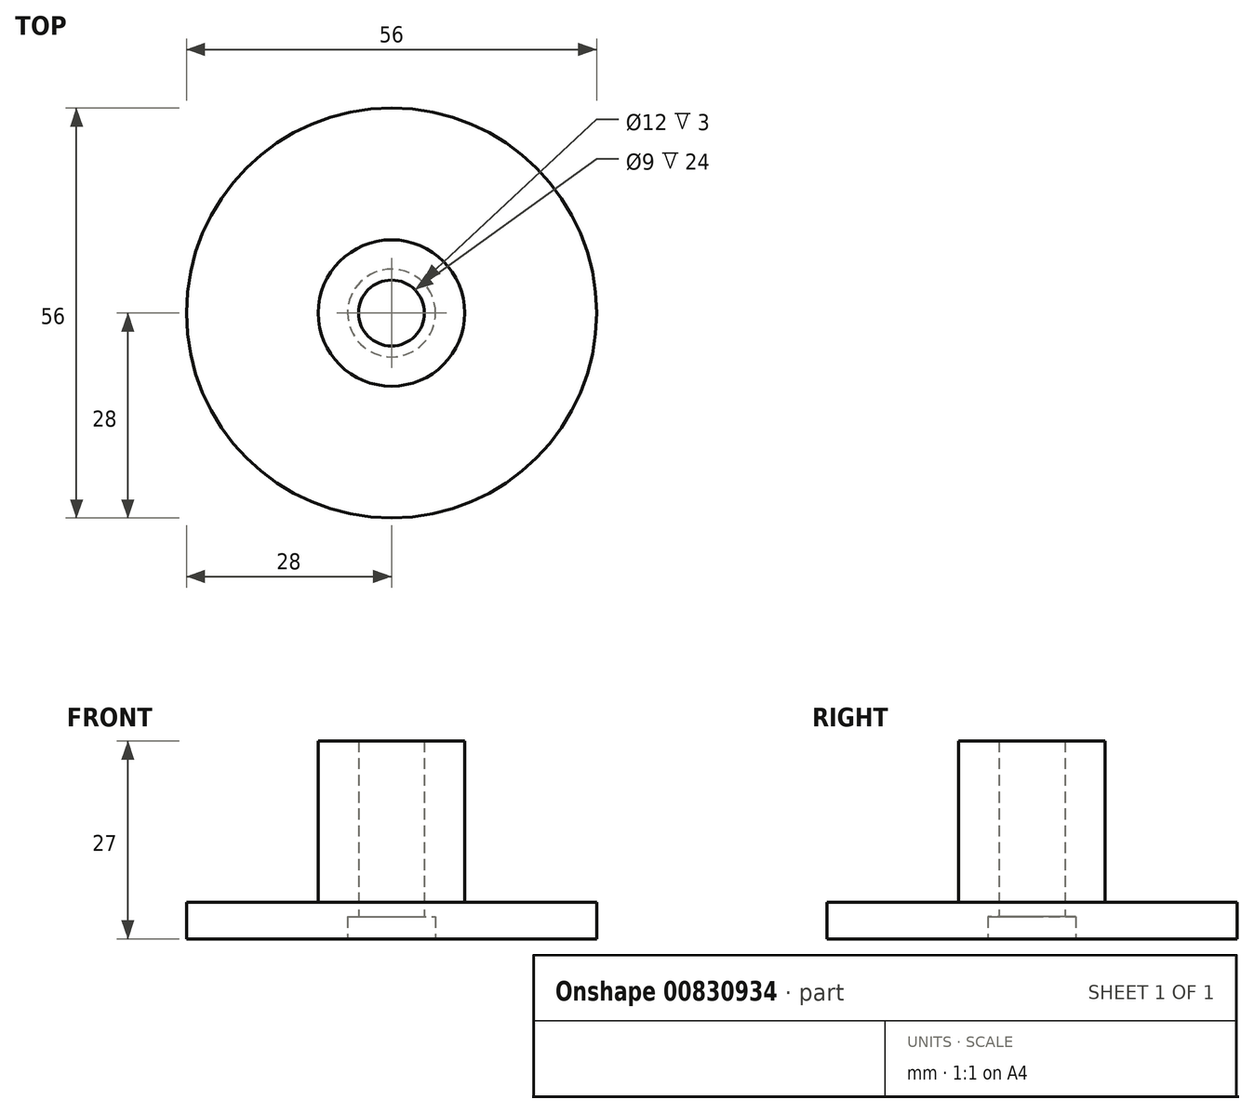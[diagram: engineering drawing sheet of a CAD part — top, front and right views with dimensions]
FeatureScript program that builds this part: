
annotation { "Feature Type Name" : "Feature", "Feature Type Description" : "" }
export const myFeature = defineFeature(function(context is Context, id is Id, definition is map)
    precondition{}
    {
        {
            var Q0;
            Q0=qCreatedBy(makeId("Top.planeOp"),FACE);
            var sketch = newSketch(context, id + "F0", { "sketchPlane" : qUnion([Q0])});
            skCircle(sketch, "E0", {"center": v(0, 0) * mm, "radius": 28 * mm});
            skSolve(sketch);
        }
        {
            var Q0;
            Q0=makeQuery(id+"F0.imprint","IMPRINT",FACE,{"disambiguationData":[TD([[makeQuery(id+"F0.imprint","IMPRINT",EDGE,{"derivedFrom":sQuery(id+"F0.wireOp",EDGE,"E0")}),1.0]])]});
            extrude(context, id + "F1", {"entities" : qUnion([Q0]), "depth" : 5 * mm, "offsetDistance" : 25 * mm});
        }
        {
            var Q0;
            Q0=makeQuery(id+"F1.opExtrude","CAP_FACE",FACE,{"disambiguationData":[OSD([sQuery(id+"F0.wireOp",EDGE,"E0")])],"isStart":false});
            var sketch = newSketch(context, id + "F2", { "sketchPlane" : qUnion([Q0])});
            skCircle(sketch, "E1", {"center": v(0, 0) * mm, "radius": 10 * mm});
            skSolve(sketch);
        }
        {
            var Q0;
            Q0 = qSketchRegion(id + "F2", true);
            extrude(context, id + "F3", {"entities" : qUnion([Q0]), "operationType" : NewBodyOperationType.ADD, "depth" : 22 * mm, "offsetDistance" : 25 * mm});
        }
        {
            var Q0;
            Q0=makeQuery(id+"F1.opExtrude","CAP_FACE",FACE,{"disambiguationData":[OSD([sQuery(id+"F0.wireOp",EDGE,"E0")])],"isStart":true});
            var sketch = newSketch(context, id + "F4", { "sketchPlane" : qUnion([Q0])});
            skCircle(sketch, "E2", {"center": v(0, 0) * mm, "radius": 6 * mm});
            skSolve(sketch);
        }
        {
            var Q0;
            Q0 = qSketchRegion(id + "F4", true);
            extrude(context, id + "F5", {"entities" : qUnion([Q0]), "operationType" : NewBodyOperationType.REMOVE, "oppositeDirection" : true, "depth" : 3 * mm, "offsetDistance" : 25 * mm});
        }
        {
            var Q0;
            Q0=makeQuery(id+"F1.opExtrude","CAP_FACE",FACE,{"disambiguationData":[OSD([sQuery(id+"F0.wireOp",EDGE,"E0")])],"isStart":true});
            var sketch = newSketch(context, id + "F6", { "sketchPlane" : qUnion([Q0])});
            skCircle(sketch, "E3", {"center": v(0, 0) * mm, "radius": 4.5 * mm});
            skSolve(sketch);
        }
        {
            var Q0;
            Q0=makeQuery(id+"F6.imprint","IMPRINT",FACE,{"disambiguationData":[TD([[makeQuery(id+"F6.imprint","IMPRINT",EDGE,{"derivedFrom":sQuery(id+"F6.wireOp",EDGE,"E3")}),1.0]])]});
            extrude(context, id + "F7", {"entities" : qUnion([Q0]), "operationType" : NewBodyOperationType.REMOVE, "oppositeDirection" : true, "depth" : 27 * mm, "offsetDistance" : 25 * mm});
        }
    });
